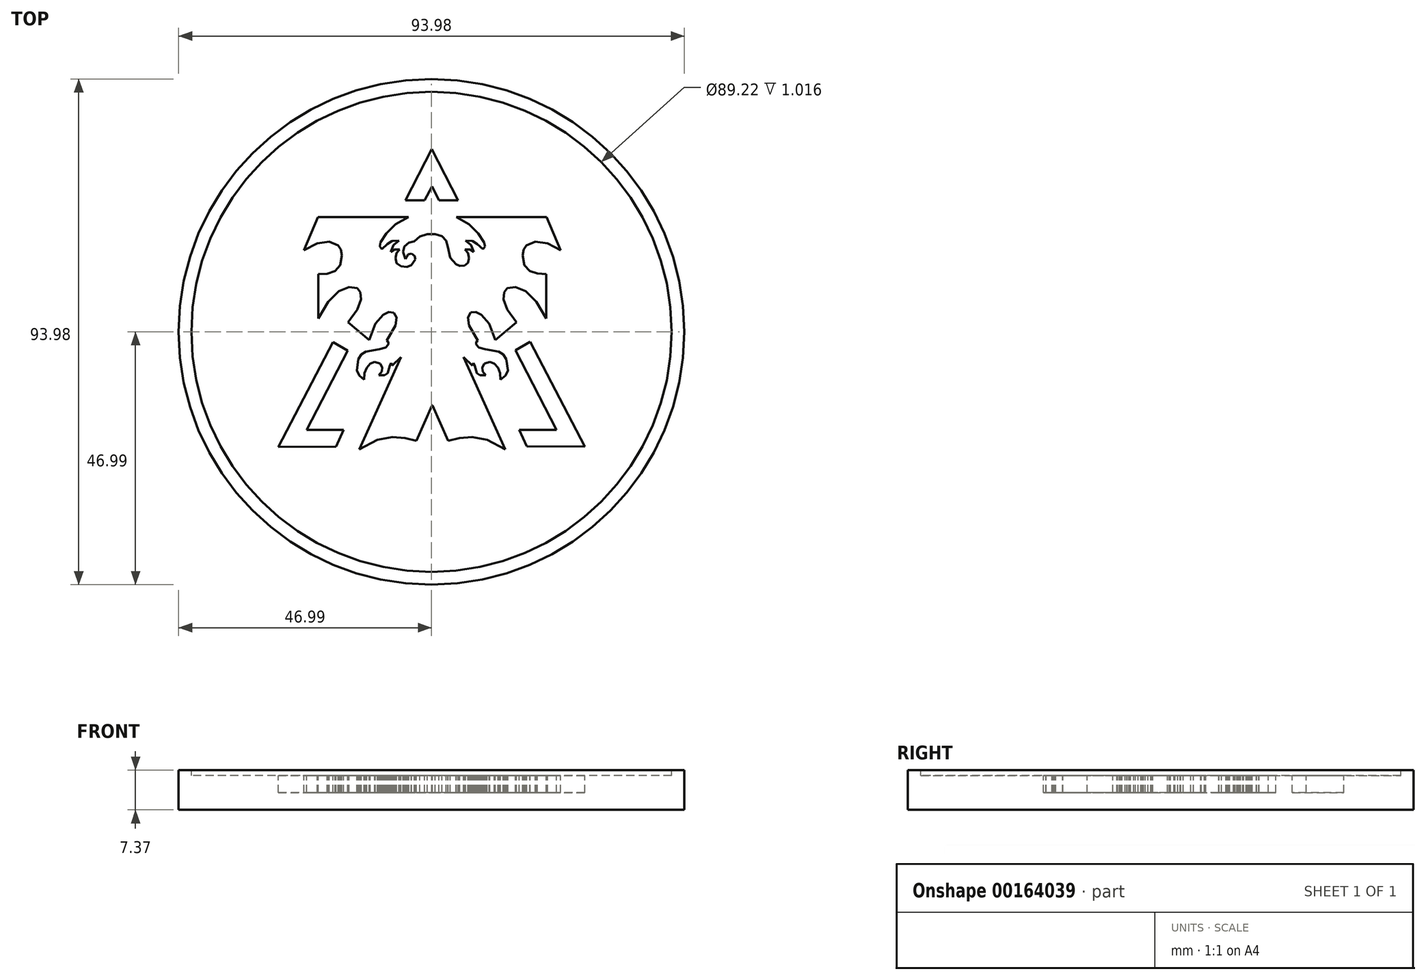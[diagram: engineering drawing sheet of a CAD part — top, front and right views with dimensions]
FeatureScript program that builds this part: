
annotation { "Feature Type Name" : "Feature", "Feature Type Description" : "" }
export const myFeature = defineFeature(function(context is Context, id is Id, definition is map)
    precondition{}
    {
        {
            var Q0;
            Q0=qCreatedBy(makeId("Front.planeOp"),FACE);
            var sketch = newSketch(context, id + "F0", { "sketchPlane" : qUnion([Q0])});
            skLineSegment(sketch, "E0", {"start": v(-47, 7.37) * mm, "end": v(-44.6, 7.37) * mm});
            skLineSegment(sketch, "E1", {"start": v(-44.6, 7.37) * mm, "end": v(-44.6, 6.35) * mm});
            skLineSegment(sketch, "E2", {"start": v(-44.6, 6.35) * mm, "end": v(0, 6.35) * mm});
            skLineSegment(sketch, "E3", {"start": v(0, 6.35) * mm, "end": v(0, 0) * mm});
            skLineSegment(sketch, "E4", {"start": v(0, 0) * mm, "end": v(-47, 0) * mm});
            skLineSegment(sketch, "E5", {"start": v(-47, 0) * mm, "end": v(-47, 7.37) * mm});
            skSolve(sketch);
        }
        {
            var Q0;
            Q0=makeQuery(id+"F0.imprint","IMPRINT",FACE,{"disambiguationData":[TD([[makeQuery(id+"F0.imprint","IMPRINT",EDGE,{"derivedFrom":sQuery(id+"F0.wireOp",EDGE,"E0")}),-1.0]])]});
            var Q1;
            Q1=sQuery(id+"F0.wireOp",EDGE,"E3");
            revolve(context, id + "F1", {"entities" : qUnion([Q0]), "axis" : qUnion([Q1]), "revolveType" : RevolveType.FULL});
        }
        {
            var Q0;
            Q0=makeQuery(id+"F1.opRevolve","SWEPT_FACE",FACE,{"disambiguationData":[OSD([sQuery(id+"F0.wireOp",EDGE,"E2")])]});
            var sketch = newSketch(context, id + "F2", { "sketchPlane" : qUnion([Q0])});
            skLineSegment(sketch, "E6", {"start": v(0.09, 27.04) * mm, "end": v(-1.28, 24.42) * mm});
            skLineSegment(sketch, "E7", {"start": v(-1.28, 24.42) * mm, "end": v(-4.84, 24.42) * mm});
            skLineSegment(sketch, "E8", {"start": v(-4.84, 24.42) * mm, "end": v(0.06, 33.99) * mm});
            skLineSegment(sketch, "E9", {"start": v(0.06, 33.99) * mm, "end": v(4.96, 24.44) * mm});
            skLineSegment(sketch, "E10", {"start": v(4.96, 24.44) * mm, "end": v(1.38, 24.42) * mm});
            skLineSegment(sketch, "E11", {"start": v(1.38, 24.42) * mm, "end": v(0.09, 27.04) * mm});
            skLineSegment(sketch, "E12", {"start": v(0.09, 27.04) * mm, "end": v(0.09, 27.04) * mm});
            skLineSegment(sketch, "E13", {"start": v(4.59, 21.37) * mm, "end": v(6.98, 19.98) * mm});
            skLineSegment(sketch, "E14", {"start": v(6.98, 19.98) * mm, "end": v(8.68, 18.27) * mm});
            skLineSegment(sketch, "E15", {"start": v(8.68, 18.27) * mm, "end": v(9.76, 16.64) * mm});
            skLineSegment(sketch, "E16", {"start": v(9.76, 16.64) * mm, "end": v(9.93, 15.85) * mm});
            skLineSegment(sketch, "E17", {"start": v(9.93, 15.85) * mm, "end": v(9.54, 15.38) * mm});
            skLineSegment(sketch, "E18", {"start": v(9.54, 15.38) * mm, "end": v(8.48, 16.31) * mm});
            skLineSegment(sketch, "E19", {"start": v(8.48, 16.31) * mm, "end": v(7.61, 16.87) * mm});
            skLineSegment(sketch, "E20", {"start": v(7.61, 16.87) * mm, "end": v(6.36, 16.96) * mm});
            skLineSegment(sketch, "E21", {"start": v(6.36, 16.96) * mm, "end": v(7.37, 16.13) * mm});
            skLineSegment(sketch, "E22", {"start": v(7.37, 16.13) * mm, "end": v(7.83, 14.85) * mm});
            skLineSegment(sketch, "E23", {"start": v(7.83, 14.85) * mm, "end": v(7.18, 15.28) * mm});
            skLineSegment(sketch, "E24", {"start": v(7.18, 15.28) * mm, "end": v(6.23, 15.28) * mm});
            skLineSegment(sketch, "E25", {"start": v(6.23, 15.28) * mm, "end": v(6.74, 14.64) * mm});
            skLineSegment(sketch, "E26", {"start": v(6.74, 14.64) * mm, "end": v(6.95, 13.71) * mm});
            skLineSegment(sketch, "E27", {"start": v(6.95, 13.71) * mm, "end": v(6.77, 12.83) * mm});
            skLineSegment(sketch, "E28", {"start": v(6.77, 12.83) * mm, "end": v(6.12, 12.3) * mm});
            skLineSegment(sketch, "E29", {"start": v(6.12, 12.3) * mm, "end": v(5.26, 12.29) * mm});
            skLineSegment(sketch, "E30", {"start": v(5.26, 12.29) * mm, "end": v(4.56, 12.6) * mm});
            skLineSegment(sketch, "E31", {"start": v(4.56, 12.6) * mm, "end": v(3.5, 13.8) * mm});
            skLineSegment(sketch, "E32", {"start": v(3.5, 13.8) * mm, "end": v(3.05, 15.83) * mm});
            skLineSegment(sketch, "E33", {"start": v(3.05, 15.83) * mm, "end": v(2.74, 16.94) * mm});
            skLineSegment(sketch, "E34", {"start": v(2.74, 16.94) * mm, "end": v(1.98, 17.78) * mm});
            skLineSegment(sketch, "E35", {"start": v(1.98, 17.78) * mm, "end": v(0.69, 18.2) * mm});
            skLineSegment(sketch, "E36", {"start": v(0.69, 18.2) * mm, "end": v(-0.8, 18.18) * mm});
            skLineSegment(sketch, "E37", {"start": v(-0.8, 18.18) * mm, "end": v(-2.2, 17.73) * mm});
            skLineSegment(sketch, "E38", {"start": v(-2.2, 17.73) * mm, "end": v(-3.18, 16.84) * mm});
            skLineSegment(sketch, "E39", {"start": v(-3.18, 16.84) * mm, "end": v(-4.24, 16.58) * mm});
            skLineSegment(sketch, "E40", {"start": v(-4.24, 16.58) * mm, "end": v(-5.01, 15.88) * mm});
            skLineSegment(sketch, "E41", {"start": v(-5.01, 15.88) * mm, "end": v(-5.3, 14.83) * mm});
            skLineSegment(sketch, "E42", {"start": v(-5.3, 14.83) * mm, "end": v(-4.88, 13.5) * mm});
            skLineSegment(sketch, "E43", {"start": v(-4.88, 13.5) * mm, "end": v(-4.32, 14.4) * mm});
            skLineSegment(sketch, "E44", {"start": v(-4.32, 14.4) * mm, "end": v(-3.68, 14.51) * mm});
            skLineSegment(sketch, "E45", {"start": v(-3.68, 14.51) * mm, "end": v(-3.16, 14.12) * mm});
            skLineSegment(sketch, "E46", {"start": v(-3.16, 14.12) * mm, "end": v(-2.98, 13.5) * mm});
            skLineSegment(sketch, "E47", {"start": v(-2.98, 13.5) * mm, "end": v(-3.76, 12.35) * mm});
            skLineSegment(sketch, "E48", {"start": v(-3.76, 12.35) * mm, "end": v(-4.6, 12.1) * mm});
            skLineSegment(sketch, "E49", {"start": v(-4.6, 12.1) * mm, "end": v(-5.67, 12.2) * mm});
            skLineSegment(sketch, "E50", {"start": v(-5.67, 12.2) * mm, "end": v(-6.5, 12.79) * mm});
            skLineSegment(sketch, "E51", {"start": v(-6.5, 12.79) * mm, "end": v(-6.72, 13.7) * mm});
            skLineSegment(sketch, "E52", {"start": v(-6.72, 13.7) * mm, "end": v(-6.48, 14.64) * mm});
            skLineSegment(sketch, "E53", {"start": v(-6.48, 14.64) * mm, "end": v(-5.94, 15.27) * mm});
            skLineSegment(sketch, "E54", {"start": v(-5.94, 15.27) * mm, "end": v(-6.9, 15.27) * mm});
            skLineSegment(sketch, "E55", {"start": v(-6.9, 15.27) * mm, "end": v(-7.55, 14.85) * mm});
            skLineSegment(sketch, "E56", {"start": v(-7.55, 14.85) * mm, "end": v(-7.08, 16.12) * mm});
            skLineSegment(sketch, "E57", {"start": v(-7.08, 16.12) * mm, "end": v(-6.07, 16.96) * mm});
            skLineSegment(sketch, "E58", {"start": v(-6.07, 16.96) * mm, "end": v(-7.32, 16.87) * mm});
            skLineSegment(sketch, "E59", {"start": v(-7.32, 16.87) * mm, "end": v(-8.2, 16.3) * mm});
            skLineSegment(sketch, "E60", {"start": v(-8.2, 16.3) * mm, "end": v(-9.26, 15.38) * mm});
            skLineSegment(sketch, "E61", {"start": v(-9.26, 15.38) * mm, "end": v(-9.64, 15.85) * mm});
            skLineSegment(sketch, "E62", {"start": v(-9.64, 15.85) * mm, "end": v(-9.47, 16.64) * mm});
            skLineSegment(sketch, "E63", {"start": v(-9.47, 16.64) * mm, "end": v(-8.4, 18.27) * mm});
            skLineSegment(sketch, "E64", {"start": v(-8.4, 18.27) * mm, "end": v(-6.7, 19.98) * mm});
            skLineSegment(sketch, "E65", {"start": v(-6.7, 19.98) * mm, "end": v(-4.3, 21.36) * mm});
            skLineSegment(sketch, "E66", {"start": v(-4.3, 21.36) * mm, "end": v(-21.12, 21.36) * mm});
            skLineSegment(sketch, "E67", {"start": v(-21.12, 21.36) * mm, "end": v(-23.7, 15.19) * mm});
            skLineSegment(sketch, "E68", {"start": v(-23.7, 15.19) * mm, "end": v(-21.26, 16.47) * mm});
            skLineSegment(sketch, "E69", {"start": v(-21.26, 16.47) * mm, "end": v(-19.02, 16.78) * mm});
            skLineSegment(sketch, "E70", {"start": v(-19.02, 16.78) * mm, "end": v(-17.36, 16.05) * mm});
            skLineSegment(sketch, "E71", {"start": v(-17.36, 16.05) * mm, "end": v(-16.86, 15.29) * mm});
            skLineSegment(sketch, "E72", {"start": v(-16.86, 15.29) * mm, "end": v(-16.65, 14.25) * mm});
            skLineSegment(sketch, "E73", {"start": v(-16.65, 14.25) * mm, "end": v(-16.96, 12.36) * mm});
            skLineSegment(sketch, "E74", {"start": v(-16.96, 12.36) * mm, "end": v(-17.95, 11.3) * mm});
            skLineSegment(sketch, "E75", {"start": v(-17.95, 11.3) * mm, "end": v(-19.4, 10.82) * mm});
            skLineSegment(sketch, "E76", {"start": v(-19.4, 10.82) * mm, "end": v(-21.05, 10.74) * mm});
            skLineSegment(sketch, "E77", {"start": v(-21.05, 10.74) * mm, "end": v(-21.03, 2.47) * mm});
            skLineSegment(sketch, "E78", {"start": v(-21.03, 2.47) * mm, "end": v(-19.2, 5.58) * mm});
            skLineSegment(sketch, "E79", {"start": v(-19.2, 5.58) * mm, "end": v(-17.2, 7.53) * mm});
            skLineSegment(sketch, "E80", {"start": v(-17.2, 7.53) * mm, "end": v(-15.34, 8.33) * mm});
            skLineSegment(sketch, "E81", {"start": v(-15.34, 8.33) * mm, "end": v(-13.79, 8.11) * mm});
            skLineSegment(sketch, "E82", {"start": v(-13.79, 8.11) * mm, "end": v(-13.21, 7.4) * mm});
            skLineSegment(sketch, "E83", {"start": v(-13.21, 7.4) * mm, "end": v(-13.11, 6.04) * mm});
            skLineSegment(sketch, "E84", {"start": v(-13.11, 6.04) * mm, "end": v(-13.78, 4.14) * mm});
            skLineSegment(sketch, "E85", {"start": v(-13.78, 4.14) * mm, "end": v(-15.52, 1.79) * mm});
            skLineSegment(sketch, "E86", {"start": v(-15.52, 1.79) * mm, "end": v(-11.59, -1.52) * mm});
            skLineSegment(sketch, "E87", {"start": v(-11.59, -1.52) * mm, "end": v(-10.43, 1.55) * mm});
            skLineSegment(sketch, "E88", {"start": v(-10.43, 1.55) * mm, "end": v(-9, 3.17) * mm});
            skLineSegment(sketch, "E89", {"start": v(-9, 3.17) * mm, "end": v(-7.93, 3.71) * mm});
            skLineSegment(sketch, "E90", {"start": v(-7.93, 3.71) * mm, "end": v(-7, 3.59) * mm});
            skLineSegment(sketch, "E91", {"start": v(-7, 3.59) * mm, "end": v(-6.47, 2.65) * mm});
            skLineSegment(sketch, "E92", {"start": v(-6.47, 2.65) * mm, "end": v(-6.7, 1.23) * mm});
            skLineSegment(sketch, "E93", {"start": v(-6.7, 1.23) * mm, "end": v(-8.34, -1.65) * mm});
            skLineSegment(sketch, "E94", {"start": v(-8.34, -1.65) * mm, "end": v(-8, -1.87) * mm});
            skLineSegment(sketch, "E95", {"start": v(-8, -1.87) * mm, "end": v(-8.02, -2.37) * mm});
            skLineSegment(sketch, "E96", {"start": v(-8.02, -2.37) * mm, "end": v(-8.55, -2.9) * mm});
            skLineSegment(sketch, "E97", {"start": v(-8.55, -2.9) * mm, "end": v(-9.73, -3.23) * mm});
            skLineSegment(sketch, "E98", {"start": v(-9.73, -3.23) * mm, "end": v(-12.22, -3.69) * mm});
            skLineSegment(sketch, "E99", {"start": v(-12.22, -3.69) * mm, "end": v(-13.04, -4.21) * mm});
            skLineSegment(sketch, "E100", {"start": v(-13.04, -4.21) * mm, "end": v(-13.62, -5.07) * mm});
            skLineSegment(sketch, "E101", {"start": v(-13.62, -5.07) * mm, "end": v(-13.89, -7.2) * mm});
            skLineSegment(sketch, "E102", {"start": v(-13.89, -7.2) * mm, "end": v(-13.45, -8.15) * mm});
            skLineSegment(sketch, "E103", {"start": v(-13.45, -8.15) * mm, "end": v(-12.53, -8.92) * mm});
            skLineSegment(sketch, "E104", {"start": v(-12.53, -8.92) * mm, "end": v(-12.48, -7.68) * mm});
            skLineSegment(sketch, "E105", {"start": v(-12.48, -7.68) * mm, "end": v(-12.05, -6.64) * mm});
            skLineSegment(sketch, "E106", {"start": v(-12.05, -6.64) * mm, "end": v(-11.37, -5.91) * mm});
            skLineSegment(sketch, "E107", {"start": v(-11.37, -5.91) * mm, "end": v(-10.58, -5.6) * mm});
            skLineSegment(sketch, "E108", {"start": v(-10.58, -5.6) * mm, "end": v(-9.51, -5.9) * mm});
            skLineSegment(sketch, "E109", {"start": v(-9.51, -5.9) * mm, "end": v(-9.14, -6.62) * mm});
            skLineSegment(sketch, "E110", {"start": v(-9.14, -6.62) * mm, "end": v(-9.22, -7.38) * mm});
            skLineSegment(sketch, "E111", {"start": v(-9.22, -7.38) * mm, "end": v(-9.8, -8.06) * mm});
            skLineSegment(sketch, "E112", {"start": v(-9.8, -8.06) * mm, "end": v(-8.74, -8.05) * mm});
            skLineSegment(sketch, "E113", {"start": v(-8.74, -8.05) * mm, "end": v(-8.13, -7.66) * mm});
            skLineSegment(sketch, "E114", {"start": v(-8.13, -7.66) * mm, "end": v(-7.78, -6.33) * mm});
            skLineSegment(sketch, "E115", {"start": v(-7.78, -6.33) * mm, "end": v(-7.52, -5.78) * mm});
            skLineSegment(sketch, "E116", {"start": v(-7.52, -5.78) * mm, "end": v(-7.34, -6.29) * mm});
            skLineSegment(sketch, "E117", {"start": v(-7.34, -6.29) * mm, "end": v(-5.67, -4.73) * mm});
            skLineSegment(sketch, "E118", {"start": v(-5.67, -4.73) * mm, "end": v(-13.4, -21.84) * mm});
            skLineSegment(sketch, "E119", {"start": v(-13.4, -21.84) * mm, "end": v(-10.07, -20.05) * mm});
            skLineSegment(sketch, "E120", {"start": v(-10.07, -20.05) * mm, "end": v(-7.27, -19.54) * mm});
            skLineSegment(sketch, "E121", {"start": v(-7.27, -19.54) * mm, "end": v(-4.89, -19.78) * mm});
            skLineSegment(sketch, "E122", {"start": v(-4.89, -19.78) * mm, "end": v(-2.8, -20.24) * mm});
            skLineSegment(sketch, "E123", {"start": v(-2.8, -20.24) * mm, "end": v(0.12, -13.66) * mm});
            skLineSegment(sketch, "E124", {"start": v(0.12, -13.66) * mm, "end": v(0.16, -13.66) * mm});
            skLineSegment(sketch, "E125", {"start": v(0.16, -13.66) * mm, "end": v(3.1, -20.24) * mm});
            skLineSegment(sketch, "E126", {"start": v(3.1, -20.24) * mm, "end": v(5.17, -19.77) * mm});
            skLineSegment(sketch, "E127", {"start": v(5.17, -19.77) * mm, "end": v(7.56, -19.53) * mm});
            skLineSegment(sketch, "E128", {"start": v(7.56, -19.53) * mm, "end": v(10.36, -20.05) * mm});
            skLineSegment(sketch, "E129", {"start": v(10.36, -20.05) * mm, "end": v(13.7, -21.84) * mm});
            skLineSegment(sketch, "E130", {"start": v(13.7, -21.84) * mm, "end": v(5.95, -4.73) * mm});
            skLineSegment(sketch, "E131", {"start": v(5.95, -4.73) * mm, "end": v(7.62, -6.28) * mm});
            skLineSegment(sketch, "E132", {"start": v(7.62, -6.28) * mm, "end": v(7.8, -5.78) * mm});
            skLineSegment(sketch, "E133", {"start": v(7.8, -5.78) * mm, "end": v(8.07, -6.33) * mm});
            skLineSegment(sketch, "E134", {"start": v(8.07, -6.33) * mm, "end": v(8.42, -7.66) * mm});
            skLineSegment(sketch, "E135", {"start": v(8.42, -7.66) * mm, "end": v(9.03, -8.04) * mm});
            skLineSegment(sketch, "E136", {"start": v(9.03, -8.04) * mm, "end": v(10.08, -8.06) * mm});
            skLineSegment(sketch, "E137", {"start": v(10.08, -8.06) * mm, "end": v(9.51, -7.38) * mm});
            skLineSegment(sketch, "E138", {"start": v(9.51, -7.38) * mm, "end": v(9.42, -6.62) * mm});
            skLineSegment(sketch, "E139", {"start": v(9.42, -6.62) * mm, "end": v(9.8, -5.9) * mm});
            skLineSegment(sketch, "E140", {"start": v(9.8, -5.9) * mm, "end": v(10.87, -5.6) * mm});
            skLineSegment(sketch, "E141", {"start": v(10.87, -5.6) * mm, "end": v(11.65, -5.9) * mm});
            skLineSegment(sketch, "E142", {"start": v(11.65, -5.9) * mm, "end": v(12.33, -6.64) * mm});
            skLineSegment(sketch, "E143", {"start": v(12.33, -6.64) * mm, "end": v(12.77, -7.68) * mm});
            skLineSegment(sketch, "E144", {"start": v(12.77, -7.68) * mm, "end": v(12.81, -8.91) * mm});
            skLineSegment(sketch, "E145", {"start": v(12.81, -8.91) * mm, "end": v(13.73, -8.15) * mm});
            skLineSegment(sketch, "E146", {"start": v(13.73, -8.15) * mm, "end": v(14.18, -7.2) * mm});
            skLineSegment(sketch, "E147", {"start": v(14.18, -7.2) * mm, "end": v(13.9, -5.07) * mm});
            skLineSegment(sketch, "E148", {"start": v(13.9, -5.07) * mm, "end": v(13.33, -4.2) * mm});
            skLineSegment(sketch, "E149", {"start": v(13.33, -4.2) * mm, "end": v(12.5, -3.68) * mm});
            skLineSegment(sketch, "E150", {"start": v(12.5, -3.68) * mm, "end": v(10.01, -3.23) * mm});
            skLineSegment(sketch, "E151", {"start": v(10.01, -3.23) * mm, "end": v(8.83, -2.9) * mm});
            skLineSegment(sketch, "E152", {"start": v(8.83, -2.9) * mm, "end": v(8.3, -2.37) * mm});
            skLineSegment(sketch, "E153", {"start": v(8.3, -2.37) * mm, "end": v(8.28, -1.87) * mm});
            skLineSegment(sketch, "E154", {"start": v(8.28, -1.87) * mm, "end": v(8.63, -1.65) * mm});
            skLineSegment(sketch, "E155", {"start": v(8.63, -1.65) * mm, "end": v(6.99, 1.24) * mm});
            skLineSegment(sketch, "E156", {"start": v(6.99, 1.24) * mm, "end": v(6.76, 2.66) * mm});
            skLineSegment(sketch, "E157", {"start": v(6.76, 2.66) * mm, "end": v(7.28, 3.59) * mm});
            skLineSegment(sketch, "E158", {"start": v(7.28, 3.59) * mm, "end": v(8.21, 3.71) * mm});
            skLineSegment(sketch, "E159", {"start": v(8.21, 3.71) * mm, "end": v(9.28, 3.18) * mm});
            skLineSegment(sketch, "E160", {"start": v(9.28, 3.18) * mm, "end": v(10.71, 1.55) * mm});
            skLineSegment(sketch, "E161", {"start": v(10.71, 1.55) * mm, "end": v(11.87, -1.52) * mm});
            skLineSegment(sketch, "E162", {"start": v(11.87, -1.52) * mm, "end": v(15.8, 1.8) * mm});
            skLineSegment(sketch, "E163", {"start": v(15.8, 1.8) * mm, "end": v(14.07, 4.15) * mm});
            skLineSegment(sketch, "E164", {"start": v(14.07, 4.15) * mm, "end": v(13.4, 6.04) * mm});
            skLineSegment(sketch, "E165", {"start": v(13.4, 6.04) * mm, "end": v(13.5, 7.4) * mm});
            skLineSegment(sketch, "E166", {"start": v(13.5, 7.4) * mm, "end": v(14.07, 8.12) * mm});
            skLineSegment(sketch, "E167", {"start": v(14.07, 8.12) * mm, "end": v(15.63, 8.33) * mm});
            skLineSegment(sketch, "E168", {"start": v(15.63, 8.33) * mm, "end": v(17.49, 7.53) * mm});
            skLineSegment(sketch, "E169", {"start": v(17.49, 7.53) * mm, "end": v(19.48, 5.58) * mm});
            skLineSegment(sketch, "E170", {"start": v(19.48, 5.58) * mm, "end": v(21.32, 2.48) * mm});
            skLineSegment(sketch, "E171", {"start": v(21.32, 2.48) * mm, "end": v(21.34, 10.75) * mm});
            skLineSegment(sketch, "E172", {"start": v(21.34, 10.75) * mm, "end": v(19.68, 10.83) * mm});
            skLineSegment(sketch, "E173", {"start": v(19.68, 10.83) * mm, "end": v(18.24, 11.3) * mm});
            skLineSegment(sketch, "E174", {"start": v(18.24, 11.3) * mm, "end": v(17.25, 12.37) * mm});
            skLineSegment(sketch, "E175", {"start": v(17.25, 12.37) * mm, "end": v(16.94, 14.25) * mm});
            skLineSegment(sketch, "E176", {"start": v(16.94, 14.25) * mm, "end": v(17.15, 15.3) * mm});
            skLineSegment(sketch, "E177", {"start": v(17.15, 15.3) * mm, "end": v(17.65, 16.06) * mm});
            skLineSegment(sketch, "E178", {"start": v(17.65, 16.06) * mm, "end": v(19.3, 16.78) * mm});
            skLineSegment(sketch, "E179", {"start": v(19.3, 16.78) * mm, "end": v(21.55, 16.47) * mm});
            skLineSegment(sketch, "E180", {"start": v(21.55, 16.47) * mm, "end": v(23.99, 15.2) * mm});
            skLineSegment(sketch, "E181", {"start": v(23.99, 15.2) * mm, "end": v(21.4, 21.37) * mm});
            skLineSegment(sketch, "E182", {"start": v(21.4, 21.37) * mm, "end": v(4.59, 21.37) * mm});
            skLineSegment(sketch, "E183", {"start": v(4.59, 21.37) * mm, "end": v(4.59, 21.37) * mm});
            skLineSegment(sketch, "E184", {"start": v(-28.49, -21.4) * mm, "end": v(-18.32, -1.88) * mm});
            skLineSegment(sketch, "E185", {"start": v(-18.32, -1.88) * mm, "end": v(-15.6, -3.47) * mm});
            skLineSegment(sketch, "E186", {"start": v(-15.6, -3.47) * mm, "end": v(-23.19, -18.23) * mm});
            skLineSegment(sketch, "E187", {"start": v(-23.19, -18.23) * mm, "end": v(-16.33, -18.23) * mm});
            skLineSegment(sketch, "E188", {"start": v(-16.33, -18.23) * mm, "end": v(-17.72, -21.3) * mm});
            skLineSegment(sketch, "E189", {"start": v(-17.72, -21.3) * mm, "end": v(-28.49, -21.4) * mm});
            skLineSegment(sketch, "E190", {"start": v(28.49, -21.36) * mm, "end": v(18.32, -1.85) * mm});
            skLineSegment(sketch, "E191", {"start": v(18.32, -1.85) * mm, "end": v(15.6, -3.44) * mm});
            skLineSegment(sketch, "E192", {"start": v(15.6, -3.44) * mm, "end": v(23.19, -18.2) * mm});
            skLineSegment(sketch, "E193", {"start": v(23.19, -18.2) * mm, "end": v(16.33, -18.2) * mm});
            skLineSegment(sketch, "E194", {"start": v(16.33, -18.2) * mm, "end": v(17.72, -21.28) * mm});
            skLineSegment(sketch, "E195", {"start": v(17.72, -21.28) * mm, "end": v(28.49, -21.36) * mm});
            skSolve(sketch);
        }
        {
            var Q0;
            Q0=makeQuery(id+"F2.imprint","IMPRINT",FACE,{"disambiguationData":[TD([[makeQuery(id+"F2.imprint","IMPRINT",EDGE,{"derivedFrom":sQuery(id+"F2.wireOp",EDGE,"E6")}),-1.0]])]});
            var Q1;
            {var subQ0=sQuery(id+"F2.wireOp",EDGE,"E14");Q1=makeQuery(id+"F2.imprint","IMPRINT",FACE,{"disambiguationData":[TD([[makeQuery(id+"F2.imprint","IMPRINT",EDGE,{"derivedFrom":subQ0}),1.0]])]});}
            var Q2;
            Q2=makeQuery(id+"F2.imprint","IMPRINT",FACE,{"disambiguationData":[TD([[makeQuery(id+"F2.imprint","IMPRINT",EDGE,{"derivedFrom":sQuery(id+"F2.wireOp",EDGE,"E190")}),1.0]])]});
            var Q3;
            Q3=makeQuery(id+"F2.imprint","IMPRINT",FACE,{"disambiguationData":[TD([[makeQuery(id+"F2.imprint","IMPRINT",EDGE,{"derivedFrom":sQuery(id+"F2.wireOp",EDGE,"E184")}),-1.0]])]});
            extrude(context, id + "F3", {"entities" : qUnion([Q0, Q1, Q2, Q3]), "operationType" : NewBodyOperationType.REMOVE, "oppositeDirection" : true, "depth" : 3.17 * mm});
        }
    });
